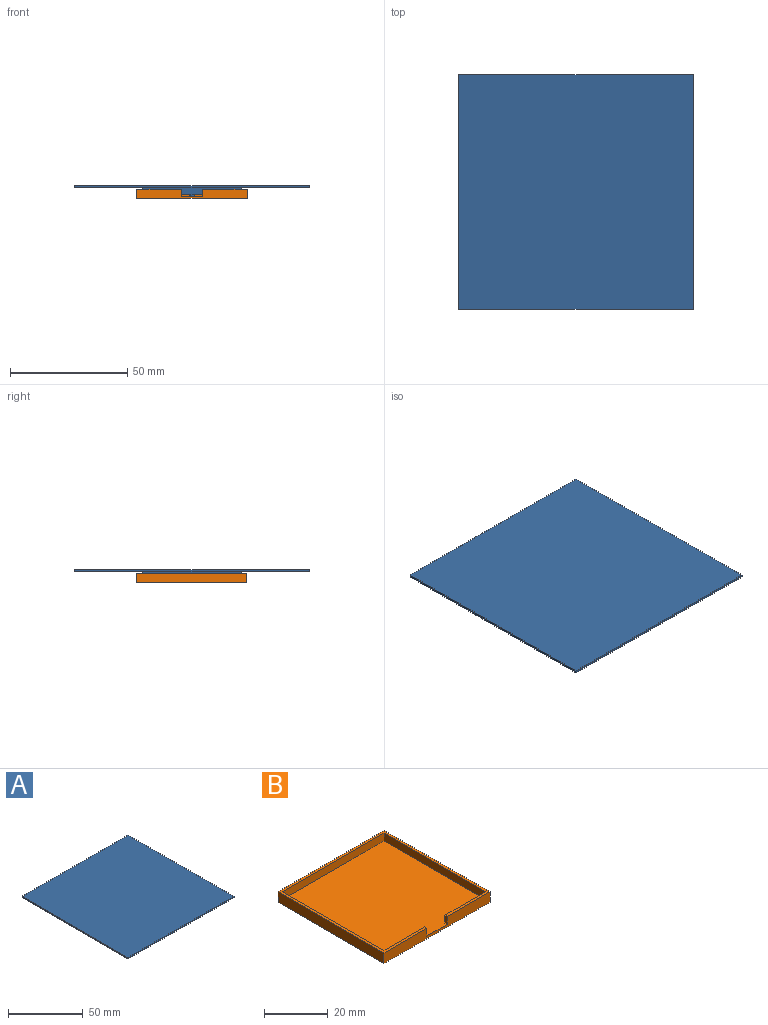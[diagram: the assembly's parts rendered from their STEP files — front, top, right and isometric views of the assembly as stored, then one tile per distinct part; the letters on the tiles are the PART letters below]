
ASSEMBLY  parts=2 mates=1
PART A: 18 faces, bbox 100x100x4.5 mm
  f0: plane 100x100mm, normal (0,0,-1), area 8236mm2, adj f1,f2,f3,f4,f6,f7,f8,f9
  f1: plane 100x1mm, normal (0,1,0), area 100mm2, adj f0,f2,f4,f5
  f2: plane 100x1mm, normal (-1,0,0), area 100mm2, adj f0,f1,f3,f5
  f3: plane 100x1mm, normal (0,-1,0), area 100mm2, adj f0,f2,f4,f5
  f4: plane 100x1mm, normal (1,0,0), area 100mm2, adj f0,f1,f3,f5
  f5: plane 100x100mm, normal (0,0,1), area 10000mm2, adj f1,f2,f3,f4
  f6: plane 42x3mm, normal (-1,0,0), area 126mm2, adj f0,f7,f9,f10
  f7: plane 42x3mm, normal (0,1,0), area 126mm2, adj f0,f6,f8,f10
  f8: plane 42x3mm, normal (1,0,0), area 126mm2, adj f0,f7,f9,f10
  f9: plane 42x3mm, normal (0,-1,0), area 126mm2, adj f0,f6,f8,f10
  f10: plane 42x42mm, normal (0,0,-1), area 164mm2, adj f6,f7,f8,f9,f11,f12,f13,f14
  f11: plane 40x3mm, normal (0,-1,0), area 120mm2, adj f10,f12,f14,f15
  f12: plane 40x3mm, normal (-1,0,0), area 120mm2, adj f10,f11,f13,f15
  f13: plane 40x3mm, normal (0,1,0), area 120mm2, adj f10,f12,f14,f15
  f14: plane 40x3mm, normal (1,0,0), area 120mm2, adj f10,f11,f13,f15
  f15: plane 40x40mm, normal (0,0,-1), area 1596.9mm2, adj f11,f12,f13,f14,f16
  f16: cylinder r=1mm len=3.5mm, axis (0,0,1), area 22mm2, adj f15,f17
  f17: plane 2x2mm, normal (0,0,-1), area 3.1mm2, adj f16
PART B: 14 faces, bbox 47x47x4 mm
  f0: plane 47x47mm, normal (0,0,1), area 175mm2, adj f1,f2,f3,f4,f5,f7,f8,f9
  f1: plane 18x3mm, normal (0,1,0), area 54mm2, adj f0,f10,f11,f12
  f2: plane 47x4mm, normal (0,1,0), area 188mm2, adj f0,f3,f5,f6
  f3: plane 47x4mm, normal (-1,0,0), area 188mm2, adj f0,f2,f4,f6
  f4: plane 47x4mm, normal (0,-1,0), area 161mm2, adj f0,f3,f5,f6,f11,f12,f13
  f5: plane 47x4mm, normal (1,0,0), area 188mm2, adj f0,f2,f4,f6
  f6: plane 47x47mm, normal (0,0,-1), area 2209mm2, adj f2,f3,f4,f5
  f7: plane 45x3mm, normal (0,-1,0), area 135mm2, adj f0,f8,f10,f11
  f8: plane 45x3mm, normal (1,0,0), area 135mm2, adj f0,f7,f9,f11
  f9: plane 18x3mm, normal (0,1,0), area 54mm2, adj f0,f8,f11,f13
  f10: plane 45x3mm, normal (-1,0,0), area 135mm2, adj f0,f1,f7,f11
  f11: plane 46x45mm, normal (0,0,1), area 2034mm2, adj f1,f4,f7,f8,f9,f10,f12,f13
  f12: plane 3x1mm, normal (-1,0,0), area 3mm2, adj f0,f1,f4,f11
  f13: plane 3x1mm, normal (1,0,0), area 3mm2, adj f0,f4,f9,f11
PLACE A t=(0.06,-0.09,2.46)mm
PLACE B t=(0.06,0.01,-2.04)mm
MATE planar A.f16 <-> B.f11  axis (0,0,-1) through (0.06,-0.09,-1.04)mm
